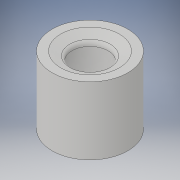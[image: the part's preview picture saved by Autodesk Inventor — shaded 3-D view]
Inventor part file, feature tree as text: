
AUTODESK INVENTOR PART (.ipt)
format: ipt  version: 2017 (Build 210142000, 142)  size: 145,408 bytes
history: native  units: in
note: dims shown in document units (in); Inventor stores cm internally (conversion verified against a paired STEP export)
features: revolve x1, sketch x1
ambient origin geometry x8: Origin, YZ Plane, XZ Plane, XY Plane, X Axis, Y Axis, Z Axis, Center Point
bodies: Solid1 (feature_tree)
feature tree (2):
  revolve  "Revolution1"  [1 undecoded]
  sketch  "Sketch1"  dims[d0=1.13in d1=3.4in d2=0.25in d3=0.1718in d5=1.0in d6=1.0in d7=90.0deg d8=0.5in d9=15.0deg d11=0.25in d12=1.25in d13=0.25in d15=0.25in d16=0.5in d17=0.5in d18=0.5in d19=2.5in d20=0.5in d22=0.375in d23=0.25in d25=0.234in d26=15.0deg d27=90.0deg]
note: 1 required parameter value undecoded (feature->parameter linkage not recoverable at this tier; creation-order binding heuristic only, values carry confidence <= 0.55)
